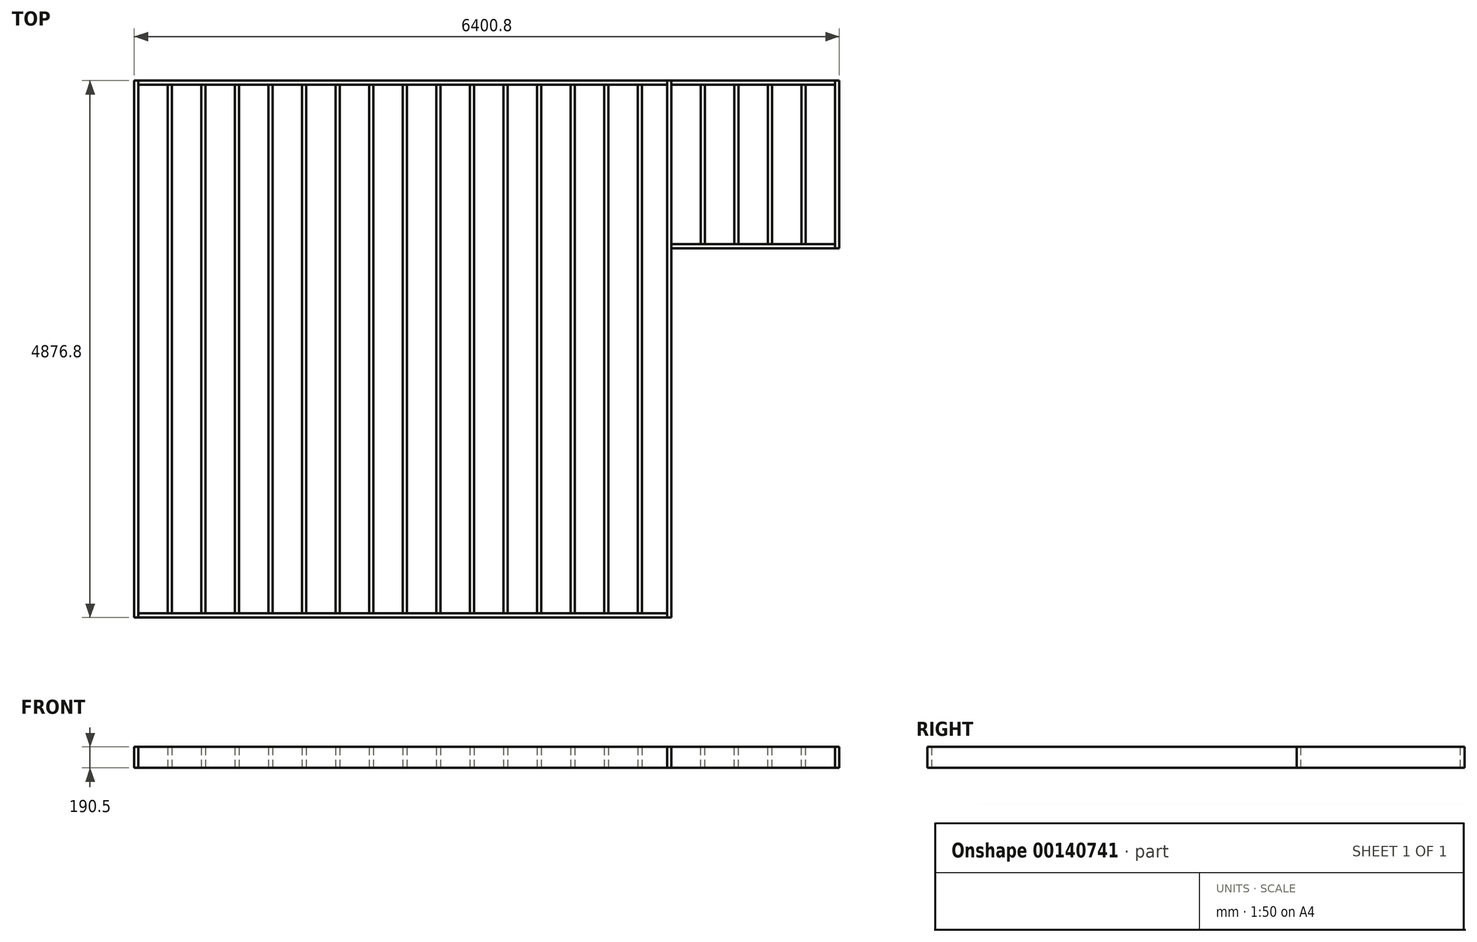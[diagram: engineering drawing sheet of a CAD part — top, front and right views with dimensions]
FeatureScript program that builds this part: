
annotation { "Feature Type Name" : "Feature", "Feature Type Description" : "" }
export const myFeature = defineFeature(function(context is Context, id is Id, definition is map)
    precondition{}
    {
        {
            var Q0;
            Q0=qCreatedBy(makeId("Top.planeOp"),FACE);
            var sketch = newSketch(context, id + "F0", { "sketchPlane" : qUnion([Q0])});
            skLineSegment(sketch, "E0.bottom", {"start": v(2438.4, 2438.4) * mm, "end": v(-2438.4, 2438.4) * mm, "construction": true});
            skLineSegment(sketch, "E0.top", {"start": v(2438.4, -2438.4) * mm, "end": v(-2438.4, -2438.4) * mm, "construction": true});
            skLineSegment(sketch, "E0.left", {"start": v(2438.4, 2438.4) * mm, "end": v(2438.4, -2438.4) * mm, "construction": true});
            skLineSegment(sketch, "E0.right", {"start": v(-2438.4, 2438.4) * mm, "end": v(-2438.4, -2438.4) * mm, "construction": true});
            skPoint(sketch, "E0.middle", {"position": v(0, 0) * mm});
            skLineSegment(sketch, "E1.bottom", {"start": v(2438.4, 2438.4) * mm, "end": v(3962.4, 2438.4) * mm, "construction": true});
            skLineSegment(sketch, "E1.top", {"start": v(2438.4, 914.4) * mm, "end": v(3962.4, 914.4) * mm, "construction": true});
            skLineSegment(sketch, "E1.left", {"start": v(2438.4, 2438.4) * mm, "end": v(2438.4, 914.4) * mm, "construction": true});
            skLineSegment(sketch, "E1.right", {"start": v(3962.4, 2438.4) * mm, "end": v(3962.4, 914.4) * mm, "construction": true});
            skSolve(sketch);
        }
        {
            var Q0;
            Q0=qCreatedBy(makeId("Right.planeOp"),FACE);
            var sketch = newSketch(context, id + "F1", { "sketchPlane" : qUnion([Q0])});
            skLineSegment(sketch, "E2.bottom", {"start": v(2438.4, 0) * mm, "end": v(2400.3, 0) * mm});
            skLineSegment(sketch, "E2.top", {"start": v(2438.4, 190.5) * mm, "end": v(2400.3, 190.5) * mm});
            skLineSegment(sketch, "E2.left", {"start": v(2438.4, 0) * mm, "end": v(2438.4, 190.5) * mm});
            skLineSegment(sketch, "E2.right", {"start": v(2400.3, 0) * mm, "end": v(2400.3, 190.5) * mm});
            skSolve(sketch);
        }
        {
            var Q0;
            Q0 = qSketchRegion(id + "F1", true);
            extrude(context, id + "F2", {"entities" : qUnion([Q0]), "oppositeDirection" : true, "depth" : 2438.4 * mm - 38.1 * mm, "hasSecondDirection" : true, "secondDirectionOppositeDirection" : false, "secondDirectionDepth" : 2438.4 * mm - 38.1 * mm});
        }
        {
            var Q0;
            Q0=makeQuery(id+"F2.opExtrude","SWEPT_BODY",BODY,{"disambiguationData":[OSD([sQuery(id+"F1.wireOp",EDGE,"E2.bottom"),sQuery(id+"F1.wireOp",EDGE,"E2.top"),sQuery(id+"F1.wireOp",EDGE,"E2.left"),sQuery(id+"F1.wireOp",EDGE,"E2.right")])]});
            var Q1;
            Q1=sQuery(id+"F0.wireOp",EDGE,"E0.right");
            transform(context, id + "F3", {"entities" : qUnion([Q0]), "transformType" : TransformType.TRANSLATION_DISTANCE, "transformDirection" : qUnion([Q1]), "distance" : 4876.8 * mm - 38.1 * mm, "makeCopy" : true});
        }
        {
            var Q0;
            Q0=makeQuery(id+"F3.opPattern","COPY",FACE,{"derivedFrom":makeQuery(id+"F2.opExtrude","SWEPT_FACE",FACE,{"disambiguationData":[OSD([sQuery(id+"F1.wireOp",EDGE,"E2.right")])]}),"instanceName":"1"});
            var sketch = newSketch(context, id + "F4", { "sketchPlane" : qUnion([Q0])});
            skLineSegment(sketch, "E3.bottom", {"start": v(-2400.3, 0) * mm, "end": v(-2438.4, 0) * mm});
            skLineSegment(sketch, "E3.top", {"start": v(-2400.3, 190.5) * mm, "end": v(-2438.4, 190.5) * mm});
            skLineSegment(sketch, "E3.left", {"start": v(-2400.3, 0) * mm, "end": v(-2400.3, 190.5) * mm});
            skLineSegment(sketch, "E3.right", {"start": v(-2438.4, 0) * mm, "end": v(-2438.4, 190.5) * mm});
            skSolve(sketch);
        }
        {
            var Q0;
            Q0 = qSketchRegion(id + "F4", true);
            var Q1;
            Q1=makeQuery(id+"F2.opExtrude","SWEPT_FACE",FACE,{"disambiguationData":[OSD([sQuery(id+"F1.wireOp",EDGE,"E2.left")])]});
            extrude(context, id + "F5", {"entities" : qUnion([Q0]), "endBound" : BoundingType.UP_TO_SURFACE, "oppositeDirection" : true, "endBoundEntityFace" : qUnion([Q1]), "depth" : 25.4 * mm});
        }
        {
            var Q0;
            Q0=makeQuery(id+"F5.opExtrude","SWEPT_BODY",BODY,{"disambiguationData":[OSD([sQuery(id+"F4.wireOp",EDGE,"E3.bottom"),sQuery(id+"F4.wireOp",EDGE,"E3.top"),sQuery(id+"F4.wireOp",EDGE,"E3.left"),sQuery(id+"F4.wireOp",EDGE,"E3.right")])]});
            var Q1;
            Q1=makeQuery(id+"F2.opExtrude","SWEPT_EDGE",EDGE,{"disambiguationData":[OSD([sQuery(id+"F1.wireOp",EDGE,"E2.top"),sQuery(id+"F1.wireOp",EDGE,"E2.left")])]});
            transform(context, id + "F6", {"entities" : qUnion([Q0]), "transformType" : TransformType.TRANSLATION_DISTANCE, "transformDirection" : qUnion([Q1]), "distance" : 4876.8 * mm - 38.1 * mm, "makeCopy" : true});
        }
        {
            var Q0;
            Q0=makeQuery(id+"F2.opExtrude","SWEPT_FACE",FACE,{"disambiguationData":[OSD([sQuery(id+"F1.wireOp",EDGE,"E2.left")])]});
            var sketch = newSketch(context, id + "F7", { "sketchPlane" : qUnion([Q0])});
            skLineSegment(sketch, "E4.bottom", {"start": v(-3924.3, 0) * mm, "end": v(-3962.4, 0) * mm});
            skLineSegment(sketch, "E4.top", {"start": v(-3924.3, 190.5) * mm, "end": v(-3962.4, 190.5) * mm});
            skLineSegment(sketch, "E4.left", {"start": v(-3924.3, 0) * mm, "end": v(-3924.3, 190.5) * mm});
            skLineSegment(sketch, "E4.right", {"start": v(-3962.4, 0) * mm, "end": v(-3962.4, 190.5) * mm});
            skSolve(sketch);
        }
        {
            var Q0;
            Q0 = qSketchRegion(id + "F7", true);
            extrude(context, id + "F8", {"entities" : qUnion([Q0]), "oppositeDirection" : true, "depth" : 1524 * mm});
        }
        {
            var Q0;
            Q0=makeQuery(id+"F6.opPattern","COPY",FACE,{"derivedFrom":makeQuery(id+"F5.opExtrude","SWEPT_FACE",FACE,{"disambiguationData":[OSD([sQuery(id+"F4.wireOp",EDGE,"E3.left")])]}),"instanceName":"1"});
            var sketch = newSketch(context, id + "F9", { "sketchPlane" : qUnion([Q0])});
            skLineSegment(sketch, "E5.bottom", {"start": v(914.4, 190.5) * mm, "end": v(952.5, 190.5) * mm});
            skLineSegment(sketch, "E5.top", {"start": v(914.4, 0) * mm, "end": v(952.5, 0) * mm});
            skLineSegment(sketch, "E5.left", {"start": v(914.4, 190.5) * mm, "end": v(914.4, 0) * mm});
            skLineSegment(sketch, "E5.right", {"start": v(952.5, 190.5) * mm, "end": v(952.5, 0) * mm});
            skSolve(sketch);
        }
        {
            var Q0;
            Q0 = qSketchRegion(id + "F9", true);
            var Q1;
            Q1=makeQuery(id+"F8.opExtrude","SWEPT_FACE",FACE,{"disambiguationData":[OSD([sQuery(id+"F7.wireOp",EDGE,"E4.left")])]});
            extrude(context, id + "F10", {"entities" : qUnion([Q0]), "endBound" : BoundingType.UP_TO_SURFACE, "endBoundEntityFace" : qUnion([Q1]), "depth" : 25.4 * mm});
        }
        {
            var Q0;
            Q0=makeQuery(id+"F10.opExtrude","SWEPT_BODY",BODY,{"disambiguationData":[OSD([sQuery(id+"F9.wireOp",EDGE,"E5.bottom"),sQuery(id+"F9.wireOp",EDGE,"E5.top"),sQuery(id+"F9.wireOp",EDGE,"E5.left"),sQuery(id+"F9.wireOp",EDGE,"E5.right")])]});
            var Q1;
            Q1=makeQuery(id+"F8.opExtrude","SWEPT_EDGE",EDGE,{"disambiguationData":[OSD([sQuery(id+"F7.wireOp",EDGE,"E4.top"),sQuery(id+"F7.wireOp",EDGE,"E4.left")])]});
            transform(context, id + "F11", {"entities" : qUnion([Q0]), "transformType" : TransformType.TRANSLATION_DISTANCE, "transformDirection" : qUnion([Q1]), "distance" : 1485.9 * mm, "makeCopy" : true});
        }
        {
            var Q0;
            Q0=makeQuery(id+"F2.opExtrude","SWEPT_FACE",FACE,{"disambiguationData":[OSD([sQuery(id+"F1.wireOp",EDGE,"E2.right")])]});
            var sketch = newSketch(context, id + "F12", { "sketchPlane" : qUnion([Q0])});
            skLineSegment(sketch, "E6.bottom", {"start": v(-2133.6, 0) * mm, "end": v(-2095.5, 0) * mm});
            skLineSegment(sketch, "E6.top", {"start": v(-2133.6, 190.5) * mm, "end": v(-2095.5, 190.5) * mm});
            skLineSegment(sketch, "E6.left", {"start": v(-2133.6, 0) * mm, "end": v(-2133.6, 190.5) * mm});
            skLineSegment(sketch, "E6.right", {"start": v(-2095.5, 0) * mm, "end": v(-2095.5, 190.5) * mm});
            skLineSegment(sketch, "E7.1.0.0", {"start": v(-1790.7, 0) * mm, "end": v(-1790.7, 190.5) * mm});
            skLineSegment(sketch, "E7.1.0.1", {"start": v(-1828.8, 0) * mm, "end": v(-1828.8, 190.5) * mm});
            skLineSegment(sketch, "E7.1.0.2", {"start": v(-1828.8, 0) * mm, "end": v(-1790.7, 0) * mm});
            skLineSegment(sketch, "E7.1.0.3", {"start": v(-1828.8, 190.5) * mm, "end": v(-1790.7, 190.5) * mm});
            skLineSegment(sketch, "E7.2.0.0", {"start": v(-1485.9, 0) * mm, "end": v(-1485.9, 190.5) * mm});
            skLineSegment(sketch, "E7.2.0.1", {"start": v(-1524, 0) * mm, "end": v(-1524, 190.5) * mm});
            skLineSegment(sketch, "E7.2.0.2", {"start": v(-1524, 0) * mm, "end": v(-1485.9, 0) * mm});
            skLineSegment(sketch, "E7.2.0.3", {"start": v(-1524, 190.5) * mm, "end": v(-1485.9, 190.5) * mm});
            skLineSegment(sketch, "E7.3.0.0", {"start": v(-1181.1, 0) * mm, "end": v(-1181.1, 190.5) * mm});
            skLineSegment(sketch, "E7.3.0.1", {"start": v(-1219.2, 0) * mm, "end": v(-1219.2, 190.5) * mm});
            skLineSegment(sketch, "E7.3.0.2", {"start": v(-1219.2, 0) * mm, "end": v(-1181.1, 0) * mm});
            skLineSegment(sketch, "E7.3.0.3", {"start": v(-1219.2, 190.5) * mm, "end": v(-1181.1, 190.5) * mm});
            skLineSegment(sketch, "E7.4.0.0", {"start": v(-876.3, 0) * mm, "end": v(-876.3, 190.5) * mm});
            skLineSegment(sketch, "E7.4.0.1", {"start": v(-914.4, 0) * mm, "end": v(-914.4, 190.5) * mm});
            skLineSegment(sketch, "E7.4.0.2", {"start": v(-914.4, 0) * mm, "end": v(-876.3, 0) * mm});
            skLineSegment(sketch, "E7.4.0.3", {"start": v(-914.4, 190.5) * mm, "end": v(-876.3, 190.5) * mm});
            skLineSegment(sketch, "E7.5.0.0", {"start": v(-571.5, 0) * mm, "end": v(-571.5, 190.5) * mm});
            skLineSegment(sketch, "E7.5.0.1", {"start": v(-609.6, 0) * mm, "end": v(-609.6, 190.5) * mm});
            skLineSegment(sketch, "E7.5.0.2", {"start": v(-609.6, 0) * mm, "end": v(-571.5, 0) * mm});
            skLineSegment(sketch, "E7.5.0.3", {"start": v(-609.6, 190.5) * mm, "end": v(-571.5, 190.5) * mm});
            skLineSegment(sketch, "E7.6.0.0", {"start": v(-266.7, 0) * mm, "end": v(-266.7, 190.5) * mm});
            skLineSegment(sketch, "E7.6.0.1", {"start": v(-304.8, 0) * mm, "end": v(-304.8, 190.5) * mm});
            skLineSegment(sketch, "E7.6.0.2", {"start": v(-304.8, 0) * mm, "end": v(-266.7, 0) * mm});
            skLineSegment(sketch, "E7.6.0.3", {"start": v(-304.8, 190.5) * mm, "end": v(-266.7, 190.5) * mm});
            skLineSegment(sketch, "E7.7.0.0", {"start": v(38.1, 0) * mm, "end": v(38.1, 190.5) * mm});
            skLineSegment(sketch, "E7.7.0.1", {"start": v(0, 0) * mm, "end": v(0, 190.5) * mm});
            skLineSegment(sketch, "E7.7.0.2", {"start": v(0, 0) * mm, "end": v(38.1, 0) * mm});
            skLineSegment(sketch, "E7.7.0.3", {"start": v(0, 190.5) * mm, "end": v(38.1, 190.5) * mm});
            skLineSegment(sketch, "E7.8.0.0", {"start": v(342.9, 0) * mm, "end": v(342.9, 190.5) * mm});
            skLineSegment(sketch, "E7.8.0.1", {"start": v(304.8, 0) * mm, "end": v(304.8, 190.5) * mm});
            skLineSegment(sketch, "E7.8.0.2", {"start": v(304.8, 0) * mm, "end": v(342.9, 0) * mm});
            skLineSegment(sketch, "E7.8.0.3", {"start": v(304.8, 190.5) * mm, "end": v(342.9, 190.5) * mm});
            skLineSegment(sketch, "E7.9.0.0", {"start": v(647.7, 0) * mm, "end": v(647.7, 190.5) * mm});
            skLineSegment(sketch, "E7.9.0.1", {"start": v(609.6, 0) * mm, "end": v(609.6, 190.5) * mm});
            skLineSegment(sketch, "E7.9.0.2", {"start": v(609.6, 0) * mm, "end": v(647.7, 0) * mm});
            skLineSegment(sketch, "E7.9.0.3", {"start": v(609.6, 190.5) * mm, "end": v(647.7, 190.5) * mm});
            skLineSegment(sketch, "E7.10.0.0", {"start": v(952.5, 0) * mm, "end": v(952.5, 190.5) * mm});
            skLineSegment(sketch, "E7.10.0.1", {"start": v(914.4, 0) * mm, "end": v(914.4, 190.5) * mm});
            skLineSegment(sketch, "E7.10.0.2", {"start": v(914.4, 0) * mm, "end": v(952.5, 0) * mm});
            skLineSegment(sketch, "E7.10.0.3", {"start": v(914.4, 190.5) * mm, "end": v(952.5, 190.5) * mm});
            skLineSegment(sketch, "E7.11.0.0", {"start": v(1257.3, 0) * mm, "end": v(1257.3, 190.5) * mm});
            skLineSegment(sketch, "E7.11.0.1", {"start": v(1219.2, 0) * mm, "end": v(1219.2, 190.5) * mm});
            skLineSegment(sketch, "E7.11.0.2", {"start": v(1219.2, 0) * mm, "end": v(1257.3, 0) * mm});
            skLineSegment(sketch, "E7.11.0.3", {"start": v(1219.2, 190.5) * mm, "end": v(1257.3, 190.5) * mm});
            skLineSegment(sketch, "E7.12.0.0", {"start": v(1562.1, 0) * mm, "end": v(1562.1, 190.5) * mm});
            skLineSegment(sketch, "E7.12.0.1", {"start": v(1524, 0) * mm, "end": v(1524, 190.5) * mm});
            skLineSegment(sketch, "E7.12.0.2", {"start": v(1524, 0) * mm, "end": v(1562.1, 0) * mm});
            skLineSegment(sketch, "E7.12.0.3", {"start": v(1524, 190.5) * mm, "end": v(1562.1, 190.5) * mm});
            skLineSegment(sketch, "E7.13.0.0", {"start": v(1866.9, 0) * mm, "end": v(1866.9, 190.5) * mm});
            skLineSegment(sketch, "E7.13.0.1", {"start": v(1828.8, 0) * mm, "end": v(1828.8, 190.5) * mm});
            skLineSegment(sketch, "E7.13.0.2", {"start": v(1828.8, 0) * mm, "end": v(1866.9, 0) * mm});
            skLineSegment(sketch, "E7.13.0.3", {"start": v(1828.8, 190.5) * mm, "end": v(1866.9, 190.5) * mm});
            skLineSegment(sketch, "E7.14.0.0", {"start": v(2171.7, 0) * mm, "end": v(2171.7, 190.5) * mm});
            skLineSegment(sketch, "E7.14.0.1", {"start": v(2133.6, 0) * mm, "end": v(2133.6, 190.5) * mm});
            skLineSegment(sketch, "E7.14.0.2", {"start": v(2133.6, 0) * mm, "end": v(2171.7, 0) * mm});
            skLineSegment(sketch, "E7.14.0.3", {"start": v(2133.6, 190.5) * mm, "end": v(2171.7, 190.5) * mm});
            skLineSegment(sketch, "E7.direction1", {"start": v(-2133.6, 0) * mm, "end": v(-1828.8, 0) * mm, "construction": true});
            skSolve(sketch);
        }
        {
            var Q0;
            Q0 = qSketchRegion(id + "F12", true);
            var Q1;
            Q1=makeQuery(id+"F3.opPattern","COPY",FACE,{"derivedFrom":makeQuery(id+"F2.opExtrude","SWEPT_FACE",FACE,{"disambiguationData":[OSD([sQuery(id+"F1.wireOp",EDGE,"E2.left")])]}),"instanceName":"1"});
            extrude(context, id + "F13", {"entities" : qUnion([Q0]), "endBound" : BoundingType.UP_TO_SURFACE, "endBoundEntityFace" : qUnion([Q1]), "depth" : 25.4 * mm});
        }
        {
            var Q0;
            Q0=makeQuery(id+"F11.opPattern","COPY",FACE,{"derivedFrom":makeQuery(id+"F10.opExtrude","SWEPT_FACE",FACE,{"disambiguationData":[OSD([sQuery(id+"F9.wireOp",EDGE,"E5.left")])]}),"instanceName":"1"});
            var sketch = newSketch(context, id + "F14", { "sketchPlane" : qUnion([Q0])});
            skLineSegment(sketch, "E8.bottom", {"start": v(2705.1, 190.5) * mm, "end": v(2743.2, 190.5) * mm});
            skLineSegment(sketch, "E8.top", {"start": v(2705.1, 0) * mm, "end": v(2743.2, 0) * mm});
            skLineSegment(sketch, "E8.left", {"start": v(2705.1, 190.5) * mm, "end": v(2705.1, 0) * mm});
            skLineSegment(sketch, "E8.right", {"start": v(2743.2, 190.5) * mm, "end": v(2743.2, 0) * mm});
            skLineSegment(sketch, "E9.1.0.0", {"start": v(3048, 190.5) * mm, "end": v(3048, 0) * mm});
            skLineSegment(sketch, "E9.1.0.1", {"start": v(3009.9, 190.5) * mm, "end": v(3009.9, 0) * mm});
            skLineSegment(sketch, "E9.1.0.2", {"start": v(3009.9, 0) * mm, "end": v(3048, 0) * mm});
            skLineSegment(sketch, "E9.1.0.3", {"start": v(3009.9, 190.5) * mm, "end": v(3048, 190.5) * mm});
            skLineSegment(sketch, "E9.2.0.0", {"start": v(3352.8, 190.5) * mm, "end": v(3352.8, 0) * mm});
            skLineSegment(sketch, "E9.2.0.1", {"start": v(3314.7, 190.5) * mm, "end": v(3314.7, 0) * mm});
            skLineSegment(sketch, "E9.2.0.2", {"start": v(3314.7, 0) * mm, "end": v(3352.8, 0) * mm});
            skLineSegment(sketch, "E9.2.0.3", {"start": v(3314.7, 190.5) * mm, "end": v(3352.8, 190.5) * mm});
            skLineSegment(sketch, "E9.3.0.0", {"start": v(3657.6, 190.5) * mm, "end": v(3657.6, 0) * mm});
            skLineSegment(sketch, "E9.3.0.1", {"start": v(3619.5, 190.5) * mm, "end": v(3619.5, 0) * mm});
            skLineSegment(sketch, "E9.3.0.2", {"start": v(3619.5, 0) * mm, "end": v(3657.6, 0) * mm});
            skLineSegment(sketch, "E9.3.0.3", {"start": v(3619.5, 190.5) * mm, "end": v(3657.6, 190.5) * mm});
            skLineSegment(sketch, "E9.direction1", {"start": v(2705.1, 0) * mm, "end": v(3009.9, 0) * mm, "construction": true});
            skSolve(sketch);
        }
        {
            var Q0;
            Q0 = qSketchRegion(id + "F14", true);
            var Q1;
            Q1=makeQuery(id+"F10.opExtrude","SWEPT_FACE",FACE,{"disambiguationData":[OSD([sQuery(id+"F9.wireOp",EDGE,"E5.right")])]});
            extrude(context, id + "F15", {"entities" : qUnion([Q0]), "endBound" : BoundingType.UP_TO_SURFACE, "endBoundEntityFace" : qUnion([Q1]), "depth" : 25.4 * mm});
        }
    });
